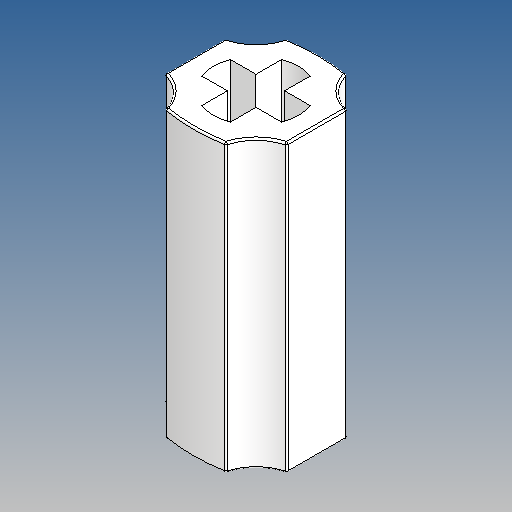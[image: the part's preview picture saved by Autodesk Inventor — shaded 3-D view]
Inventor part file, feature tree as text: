
AUTODESK INVENTOR PART (.ipt)
format: ipt  version: 2025 (Build 290162010, 162A)  size: 185,344 bytes
history: native  units: in
note: dims shown in document units (in); Inventor stores cm internally (conversion verified against a paired STEP export)
features: extrude x2, sketch x1, fillet x1
ambient origin geometry x8: Origin, YZ Plane, XZ Plane, XY Plane, X Axis, Y Axis, Z Axis, Center Point
bodies: Solid1 (feature_tree)
feature tree (4):
  sketch  "Sketch2"  dims[d0=0.1873in d1=0.2772in d2=0.315in d4=0.063in d5=0.6299in d6=0.0in d19=0.0039in d20=0.189in d21=0.7441in d22=0.2677in d23=0.0079in d24=0.0in d25=0.0in d26=0.0in d27=0.0in d28=0.0in]
  extrude  "Extrusion1"  Depth=0.0079in
  extrude  "Extrusion3"  Depth=0.315in
  fillet  "Fillet1"  Radius=0.063in
